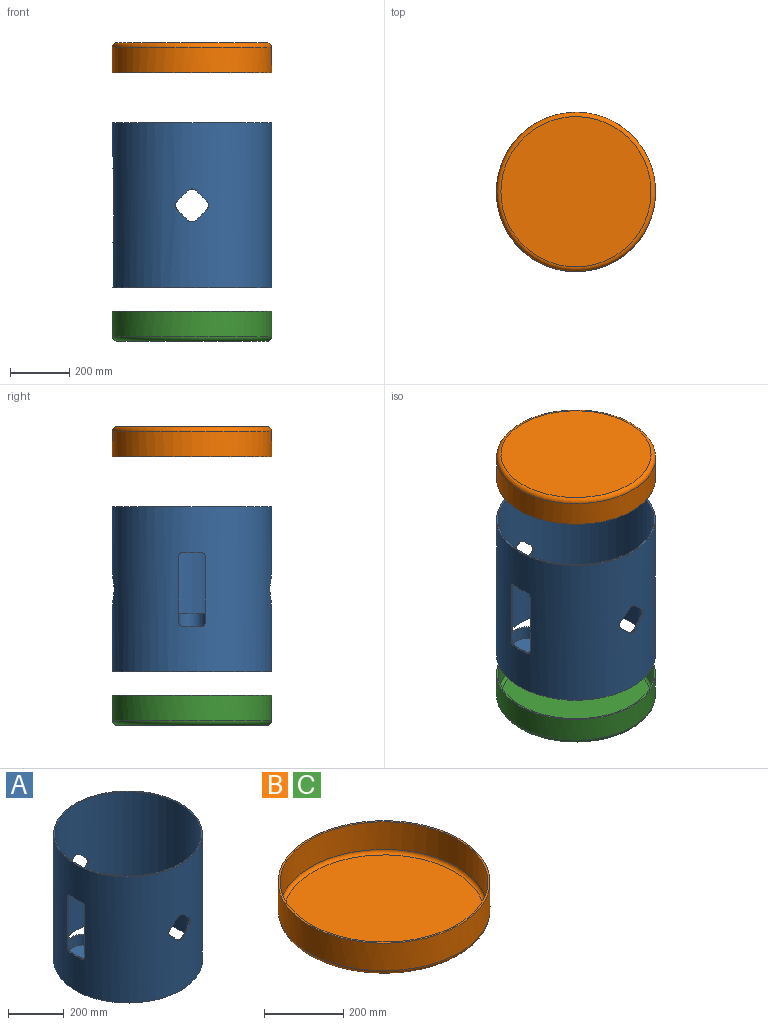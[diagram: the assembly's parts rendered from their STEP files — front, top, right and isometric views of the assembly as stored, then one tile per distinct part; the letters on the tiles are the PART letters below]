
ASSEMBLY  parts=3 mates=2
PART A: 36 faces, bbox 535x535x555 mm
  f0: plane 100x73.82mm, normal (0,0,1), area 980.1mm2, adj f2,f21,f25,f29,f30,f31,f34
  f1: cylinder r=267.5mm len=555mm, axis (0,0,1), area 894822.6mm2, adj f3,f4,f5,f6,f7,f8,f9,f10
  f2: cylinder r=262.5mm len=555mm, axis (0,0,1), area 876095.6mm2, adj f0,f3,f4,f5,f6,f7,f8,f9
  f3: plane 535x535mm, normal (0,0,-1), area 8325.2mm2, adj f1,f2
  f4: plane 535x535mm, normal (0,0,1), area 8325.2mm2, adj f1,f2
  f5: cylinder r=20mm len=28.28mm, axis (0,1,0), area 160.4mm2, adj f1,f2,f6,f12
  f6: plane 35.36x35.36mm, normal (-0.71,0,0.71), area 252mm2, adj f1,f2,f5,f7
  f7: cylinder r=20mm len=28.28mm, axis (0,1,0), area 157.2mm2, adj f1,f2,f6,f8
  f8: plane 35.36x35.36mm, normal (0.71,0,0.71), area 252mm2, adj f1,f2,f7,f9
  f9: cylinder r=20mm len=28.28mm, axis (0,1,0), area 160.4mm2, adj f1,f2,f8,f10
  f10: plane 35.36x35.36mm, normal (0.71,0,-0.71), area 252mm2, adj f1,f2,f9,f11
  f11: cylinder r=20mm len=28.28mm, axis (0,1,0), area 157.2mm2, adj f1,f2,f10,f12
  f12: plane 35.36x35.36mm, normal (-0.71,0,-0.71), area 252mm2, adj f1,f2,f5,f11
  f13: plane 35.36x35.36mm, normal (-0.71,0,-0.71), area 252mm2, adj f1,f2,f14,f20
  f14: cylinder r=20mm len=28.28mm, axis (0,1,0), area 157.2mm2, adj f1,f2,f13,f15
  f15: plane 35.36x35.36mm, normal (0.71,0,-0.71), area 252mm2, adj f1,f2,f14,f16
  f16: cylinder r=20mm len=28.28mm, axis (0,1,0), area 160.4mm2, adj f1,f2,f15,f17
  f17: plane 35.36x35.36mm, normal (0.71,0,0.71), area 252mm2, adj f1,f2,f16,f18
  f18: cylinder r=20mm len=28.28mm, axis (0,1,0), area 157.2mm2, adj f1,f2,f17,f19
  f19: plane 35.36x35.36mm, normal (-0.71,0,0.71), area 252mm2, adj f1,f2,f18,f20
  f20: cylinder r=20mm len=28.28mm, axis (0,1,0), area 160.4mm2, adj f1,f2,f13,f19
  f21: plane 237.5x30.88mm, normal (0,-1,0), area 2277.7mm2, adj f0,f1,f2,f22,f28,f33,f34,f35
  f22: cylinder r=15mm len=15mm, axis (1,0,0), area 119.2mm2, adj f1,f2,f21,f23
  f23: plane 60x6.72mm, normal (0,0,-1), area 300.6mm2, adj f1,f2,f22,f24
  f24: cylinder r=15mm len=15mm, axis (1,0,0), area 119.2mm2, adj f1,f2,f23,f25
  f25: plane 237.5x30.88mm, normal (0,1,0), area 2277.7mm2, adj f0,f1,f2,f24,f26,f33,f34,f35
  f26: cylinder r=15mm len=15mm, axis (1,0,0), area 119.2mm2, adj f1,f25,f27,f33
  f27: plane 60x6.72mm, normal (0,0,1), area 300.6mm2, adj f1,f26,f28,f33
  f28: cylinder r=15mm len=15mm, axis (1,0,0), area 119.2mm2, adj f1,f21,f27,f33
  f29: plane 50x25mm, normal (0,1,0), area 1250mm2, adj f0,f2,f31,f32
  f30: plane 50x25mm, normal (0,-1,0), area 1250mm2, adj f0,f2,f31,f32
  f31: cylinder r=50.05mm len=100mm, axis (0,0,1), area 7646.7mm2, adj f0,f29,f30,f32
  f32: plane 100x77.71mm, normal (0,0,-1), area 6540.7mm2, adj f2,f29,f30,f31
  f33: cylinder r=262.5mm len=90mm, axis (0,0,1), area 323.9mm2, adj f21,f25,f26,f27,f28,f35
  f34: cylinder r=45.05mm len=90mm, axis (0,0,1), area 6185.1mm2, adj f0,f21,f25,f35
  f35: plane 90x72.71mm, normal (0,0,1), area 5560.6mm2, adj f21,f25,f33,f34
PART B: 7 faces, bbox 579.1x579.1x100 mm
  f0: plane 505x505mm, normal (0,0,-1), area 200296.2mm2, adj f2
  f1: cylinder r=267.5mm len=535mm, axis (0,0,1), area 142863.9mm2, adj f2,f3
  f2: torus R=252.5mm, axis (0,0,1), area 38794.8mm2, adj f0,f1
  f3: plane 535x535mm, normal (0,0,1), area 8325.2mm2, adj f1,f5
  f4: plane 505x505mm, normal (0,0,1), area 200296.2mm2, adj f6
  f5: cylinder r=262.5mm len=525mm, axis (0,0,1), area 140193.6mm2, adj f3,f6
  f6: torus R=252.5mm, axis (0,0,1), area 25549.1mm2, adj f4,f5
PART C: same geometry as B
PLACE A t=(-120.55,101.14,-766.13)mm
PLACE B rot(axis=(0,1,0),180deg) t=(-120.55,101.14,158.38)mm
PLACE C t=(-120.55,101.14,-845.28)mm
MATE slider B.f1 <-> A.f1  axis (0,0,-1) through (-120.55,101.14,100.88)mm
MATE slider A.f1 <-> C.f1  axis (0,0,1) through (-120.55,101.14,-388.63)mm
